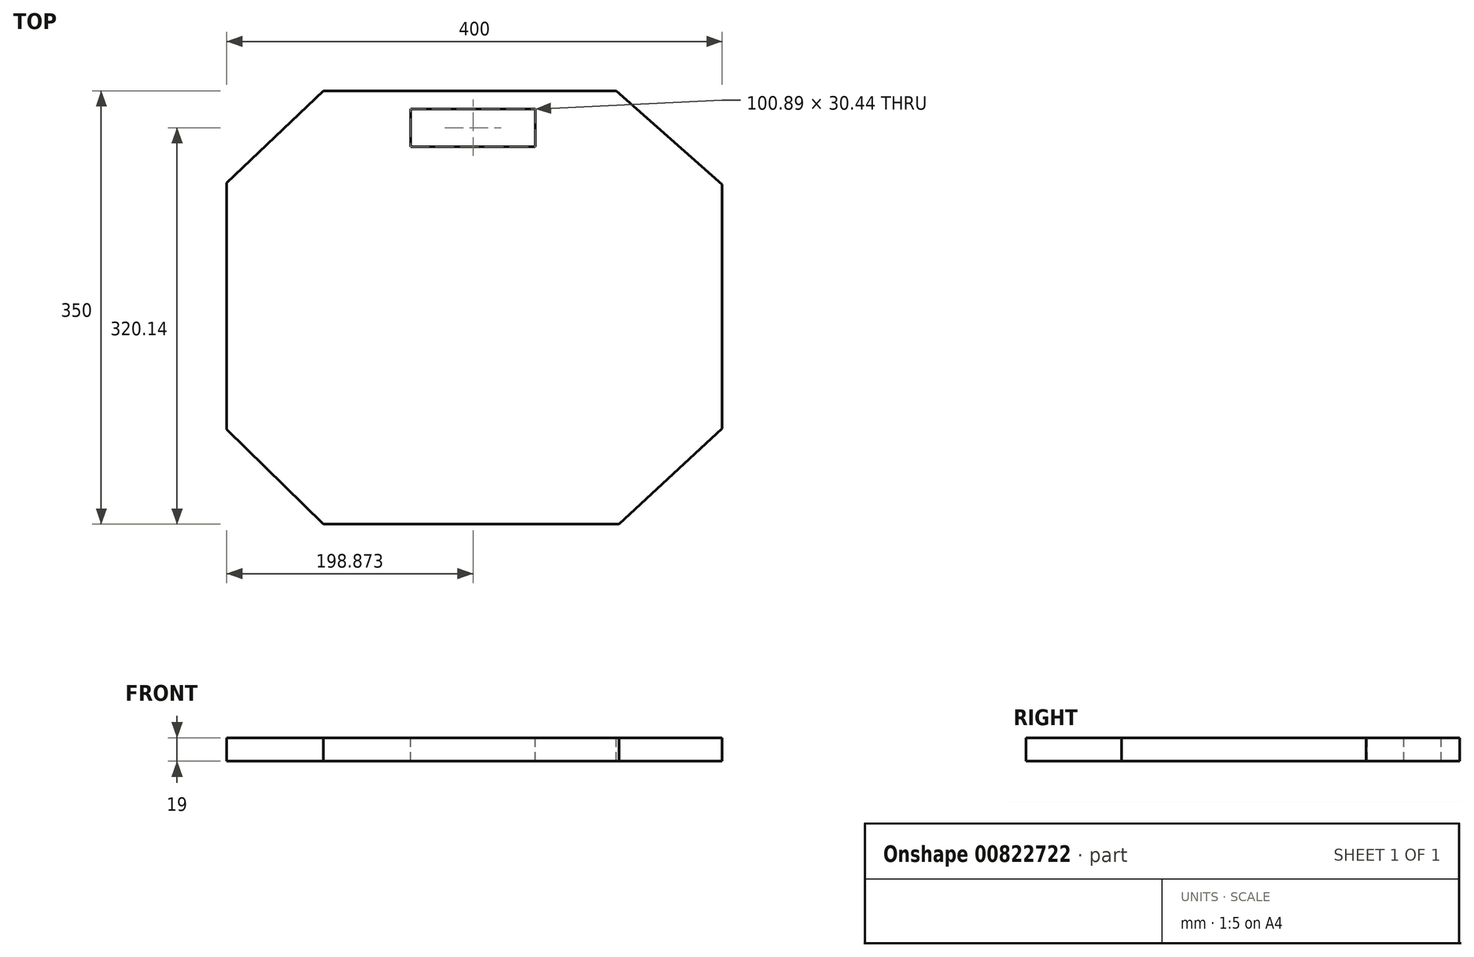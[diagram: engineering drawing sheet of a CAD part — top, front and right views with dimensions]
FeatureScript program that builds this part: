
annotation { "Feature Type Name" : "Feature", "Feature Type Description" : "" }
export const myFeature = defineFeature(function(context is Context, id is Id, definition is map)
    precondition{}
    {
        {
            var Q0;
            Q0=qCreatedBy(makeId("Top.planeOp"),FACE);
            var sketch = newSketch(context, id + "F0", { "sketchPlane" : qUnion([Q0])});
            skLineSegment(sketch, "E0.bottom", {"start": v(-200, -175) * mm, "end": v(200, -175) * mm});
            skLineSegment(sketch, "E0.top", {"start": v(-200, 175) * mm, "end": v(200, 175) * mm});
            skLineSegment(sketch, "E0.left", {"start": v(-200, -175) * mm, "end": v(-200, 175) * mm});
            skLineSegment(sketch, "E0.right", {"start": v(200, -175) * mm, "end": v(200, 175) * mm});
            skPoint(sketch, "E0.middle", {"position": v(0, 0) * mm});
            skSolve(sketch);
        }
        {
            var Q0;
            Q0 = qSketchRegion(id + "F0", true);
            extrude(context, id + "F1", {"entities" : qUnion([Q0]), "depth" : 19 * mm, "offsetDistance" : 25 * mm});
        }
        {
            var Q0;
            Q0=makeQuery(id+"F1.opExtrude","CAP_FACE",FACE,{"disambiguationData":[OSD([sQuery(id+"F0.wireOp",EDGE,"E0.bottom"),sQuery(id+"F0.wireOp",EDGE,"E0.top"),sQuery(id+"F0.wireOp",EDGE,"E0.left"),sQuery(id+"F0.wireOp",EDGE,"E0.right")])],"isStart":false});
            var sketch = newSketch(context, id + "F2", { "sketchPlane" : qUnion([Q0])});
            skLineSegment(sketch, "E1", {"start": v(-200, 100.61) * mm, "end": v(-122.03, 175) * mm});
            skLineSegment(sketch, "E2", {"start": v(114.7, 175) * mm, "end": v(200, 99.48) * mm});
            skLineSegment(sketch, "E3", {"start": v(200, -97.8) * mm, "end": v(116.96, -175) * mm});
            skLineSegment(sketch, "E4", {"start": v(-122.03, -175) * mm, "end": v(-200, -98.36) * mm});
            skSolve(sketch);
        }
        {
            var Q0;
            {var subQ0=sQuery(id+"F2.wireOp",EDGE,"E1");Q0=makeQuery(id+"F2.imprint","IMPRINT",FACE,{"disambiguationData":[TD([[makeQuery(id+"F2.imprint","IMPRINT",EDGE,{"derivedFrom":subQ0}),1.0]])]});}
            var Q1;
            {var subQ0=sQuery(id+"F2.wireOp",EDGE,"E2");Q1=makeQuery(id+"F2.imprint","IMPRINT",FACE,{"disambiguationData":[TD([[makeQuery(id+"F2.imprint","IMPRINT",EDGE,{"derivedFrom":subQ0}),1.0]])]});}
            var Q2;
            {var subQ0=sQuery(id+"F2.wireOp",EDGE,"E3");Q2=makeQuery(id+"F2.imprint","IMPRINT",FACE,{"disambiguationData":[TD([[makeQuery(id+"F2.imprint","IMPRINT",EDGE,{"derivedFrom":subQ0}),1.0]])]});}
            var Q3;
            {var subQ0=sQuery(id+"F2.wireOp",EDGE,"E4");Q3=makeQuery(id+"F2.imprint","IMPRINT",FACE,{"disambiguationData":[TD([[makeQuery(id+"F2.imprint","IMPRINT",EDGE,{"derivedFrom":subQ0}),1.0]])]});}
            extrude(context, id + "F3", {"entities" : qUnion([Q0, Q1, Q2, Q3]), "operationType" : NewBodyOperationType.REMOVE, "endBound" : BoundingType.THROUGH_ALL, "oppositeDirection" : true, "depth" : 25 * mm, "offsetDistance" : 25 * mm});
        }
        {
            var Q0;
            Q0=makeQuery(id+"F1.opExtrude","CAP_FACE",FACE,{"disambiguationData":[OSD([sQuery(id+"F0.wireOp",EDGE,"E0.bottom"),sQuery(id+"F0.wireOp",EDGE,"E0.top"),sQuery(id+"F0.wireOp",EDGE,"E0.left"),sQuery(id+"F0.wireOp",EDGE,"E0.right")])],"isStart":false});
            var sketch = newSketch(context, id + "F4", { "sketchPlane" : qUnion([Q0])});
            skLineSegment(sketch, "E5", {"start": v(-51.57, 129.92) * mm, "end": v(-51.57, 160.36) * mm});
            skLineSegment(sketch, "E6", {"start": v(-51.57, 160.36) * mm, "end": v(39.74, 160.36) * mm});
            skLineSegment(sketch, "E7", {"start": v(39.74, 160.36) * mm, "end": v(49.32, 160.36) * mm});
            skLineSegment(sketch, "E8", {"start": v(49.32, 160.36) * mm, "end": v(49.32, 129.92) * mm});
            skLineSegment(sketch, "E9", {"start": v(49.32, 129.92) * mm, "end": v(-51.57, 129.92) * mm});
            skSolve(sketch);
        }
        {
            var Q0;
            Q0=makeQuery(id+"F4.imprint","IMPRINT",FACE,{"disambiguationData":[TD([[makeQuery(id+"F4.imprint","IMPRINT",EDGE,{"derivedFrom":sQuery(id+"F4.wireOp",EDGE,"E5")}),-1.0]])]});
            extrude(context, id + "F5", {"entities" : qUnion([Q0]), "operationType" : NewBodyOperationType.REMOVE, "endBound" : BoundingType.THROUGH_ALL, "oppositeDirection" : true, "depth" : 25 * mm, "offsetDistance" : 25 * mm});
        }
    });
